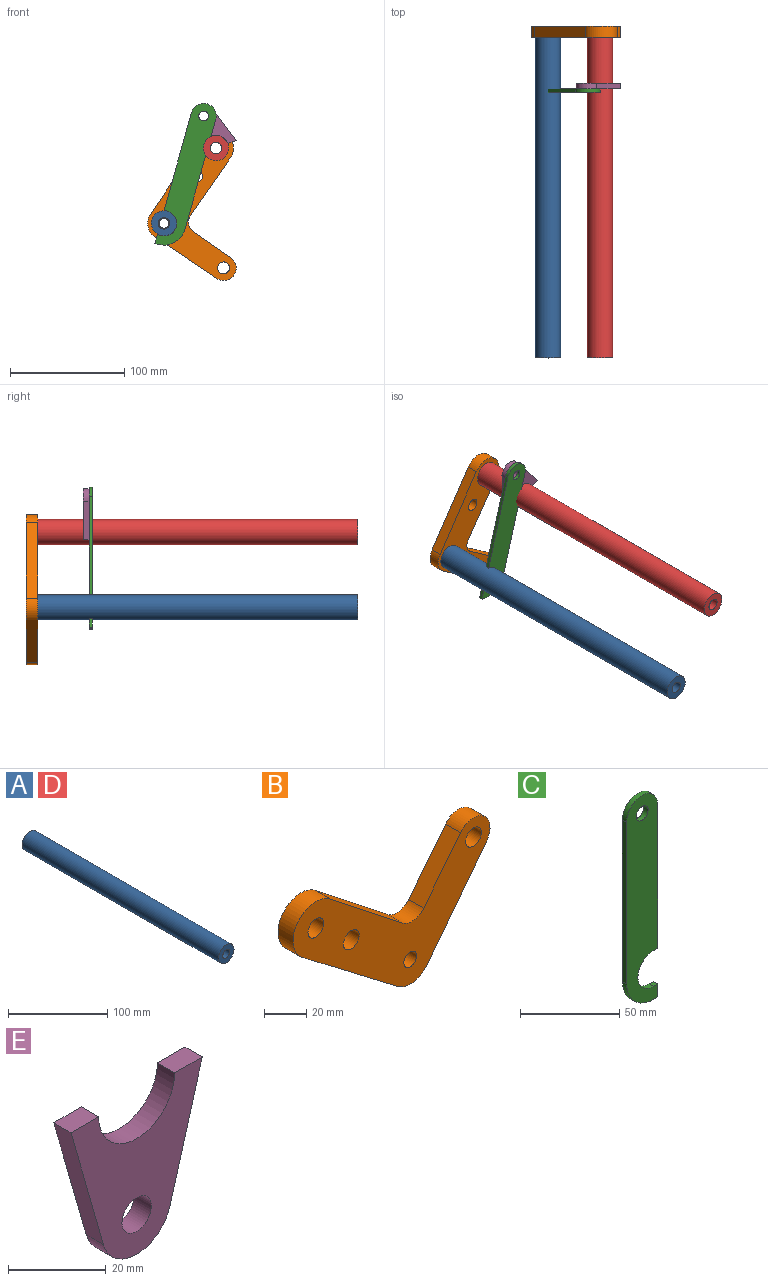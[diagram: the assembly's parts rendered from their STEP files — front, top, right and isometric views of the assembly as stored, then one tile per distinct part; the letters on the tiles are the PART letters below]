
ASSEMBLY  parts=5 mates=5
PART A: 4 faces, bbox 22x280x22 mm
  f0: cylinder r=5mm len=280mm, axis (0,-1,0), area 8796.5mm2, adj f2,f3
  f1: cylinder r=11mm len=280mm, axis (0,-1,0), area 19352.2mm2, adj f2,f3
  f2: plane 22x22mm, normal (0,1,0), area 301.6mm2, adj f0,f1
  f3: plane 22x22mm, normal (0,-1,0), area 301.6mm2, adj f0,f1
PART B: 14 faces, bbox 131.3x10x79 mm
  f0: plane 63.47x48.69mm, normal (-0.61,0,-0.79), area 799.9mm2, adj f1,f10,f12,f13
  f1: cylinder r=14.25mm len=19.97mm, axis (0,-1,0), area 223.7mm2, adj f0,f2,f12,f13
  f2: plane 51.47x39.57mm, normal (0.79,0,-0.61), area 649.2mm2, adj f1,f3,f12,f13
  f3: cylinder r=11mm len=19.64mm, axis (0,-1,0), area 344.3mm2, adj f2,f4,f12,f13
  f4: plane 31.19x24.56mm, normal (-0.79,0,0.62), area 397mm2, adj f3,f5,f12,f13
  f5: cylinder r=10mm len=14.04mm, axis (0,-1,0), area 157.1mm2, adj f4,f6,f12,f13
  f6: plane 48.32x38.04mm, normal (0.62,0,0.79), area 615mm2, adj f5,f10,f12,f13
  f7: cylinder r=4.25mm len=10mm, axis (0,-1,0), area 267mm2, adj f12,f13
  f8: cylinder r=5.25mm len=10.5mm, axis (0,-1,0), area 329.9mm2, adj f12,f13
  f9: cylinder r=5.25mm len=10.5mm, axis (0,-1,0), area 329.9mm2, adj f12,f13
  f10: cylinder r=15.25mm len=27.35mm, axis (0,-1,0), area 481mm2, adj f0,f6,f12,f13
  f11: cylinder r=5.25mm len=10.5mm, axis (0,-1,0), area 329.9mm2, adj f12,f13
  f12: plane 131.25x78.99mm, normal (0,1,0), area 4143.6mm2, adj f0,f1,f2,f3,f4,f5,f6,f7
  f13: plane 131.25x78.99mm, normal (0,-1,0), area 4143.6mm2, adj f0,f1,f2,f3,f4,f5,f6,f7
PART C: 12 faces, bbox 22x3x129.7 mm
  f0: cylinder r=11mm len=22mm, axis (0,1,0), area 103.7mm2, adj f1,f9,f10,f11
  f1: plane 3x3mm, normal (0,0,-1), area 9mm2, adj f0,f2,f10,f11
  f2: plane 88.68x3mm, normal (1,0,0), area 266mm2, adj f1,f3,f10,f11
  f3: cylinder r=11mm len=22mm, axis (0,1,0), area 103.7mm2, adj f2,f4,f10,f11
  f4: plane 99.68x3mm, normal (-1,0,0), area 299mm2, adj f3,f5,f10,f11
  f5: cylinder r=19mm len=19mm, axis (0,1,0), area 89.5mm2, adj f4,f6,f10,f11
  f6: plane 3x3mm, normal (0,0,-1), area 9mm2, adj f5,f7,f10,f11
  f7: plane 8x3mm, normal (1,0,0), area 24mm2, adj f6,f9,f10,f11
  f8: cylinder r=4.25mm len=8.5mm, axis (0,1,0), area 80.1mm2, adj f10,f11
  f9: plane 3x3mm, normal (0,0,1), area 9mm2, adj f0,f7,f10,f11
  f10: plane 129.68x22mm, normal (0,-1,0), area 2410.7mm2, adj f0,f1,f2,f3,f4,f5,f6,f7
  f11: plane 129.68x22mm, normal (0,1,0), area 2410.7mm2, adj f0,f1,f2,f3,f4,f5,f6,f7
PART D: same geometry as A
PART E: 9 faces, bbox 38x5x40 mm
  f0: cylinder r=10mm len=19.23mm, axis (0,1,0), area 129.2mm2, adj f1,f6,f7,f8
  f1: plane 32.76x9.39mm, normal (0.96,0,-0.28), area 170.4mm2, adj f0,f2,f7,f8
  f2: plane 8x5mm, normal (0,0,1), area 40mm2, adj f1,f3,f7,f8
  f3: cylinder r=11mm len=22mm, axis (0,1,0), area 172.8mm2, adj f2,f4,f7,f8
  f4: plane 8x5mm, normal (0,0,1), area 40mm2, adj f3,f6,f7,f8
  f5: cylinder r=4.25mm len=8.5mm, axis (0,1,0), area 133.5mm2, adj f7,f8
  f6: plane 32.76x9.39mm, normal (-0.96,0,-0.28), area 170.4mm2, adj f0,f4,f7,f8
  f7: plane 40x38mm, normal (0,-1,0), area 793.1mm2, adj f0,f1,f2,f3,f4,f5,f6
  f8: plane 40x38mm, normal (0,1,0), area 793.1mm2, adj f0,f1,f2,f3,f4,f5,f6
PLACE A rot(axis=(0.73,0,-0.68),180deg) t=(-95.79,0.26,-238.57)mm
PLACE B rot(axis=(0,1,0),86.4deg) t=(-50.34,0.26,-172.73)mm
PLACE C rot(axis=(-0.14,0,-0.99),180deg) t=(-61.17,-47.74,-144.75)mm
PLACE D rot(axis=(-0.63,0,0.77),180deg) t=(-50.34,0.26,-172.73)mm
PLACE E rot(axis=(0,1,0),158.8deg) t=(-61.17,-39.74,-144.75)mm
MATE revolute C.f0 <-> A.f1  axis (0,1,0) through (-95.79,-44.74,-238.57)mm
MATE revolute D.f0 <-> B.f9  axis (0,1,0) through (-50.34,0.26,-172.73)mm
MATE revolute E.f3 <-> B.f10  axis (0,1,0) through (-50.34,-39.74,-172.73)mm
MATE fastened A.f0 <-> B.f1  axis (0,1,0) through (-95.79,0.26,-238.57)mm
MATE revolute C.f3 <-> E.f5  axis (0,1,0) through (-61.17,-44.74,-144.75)mm
